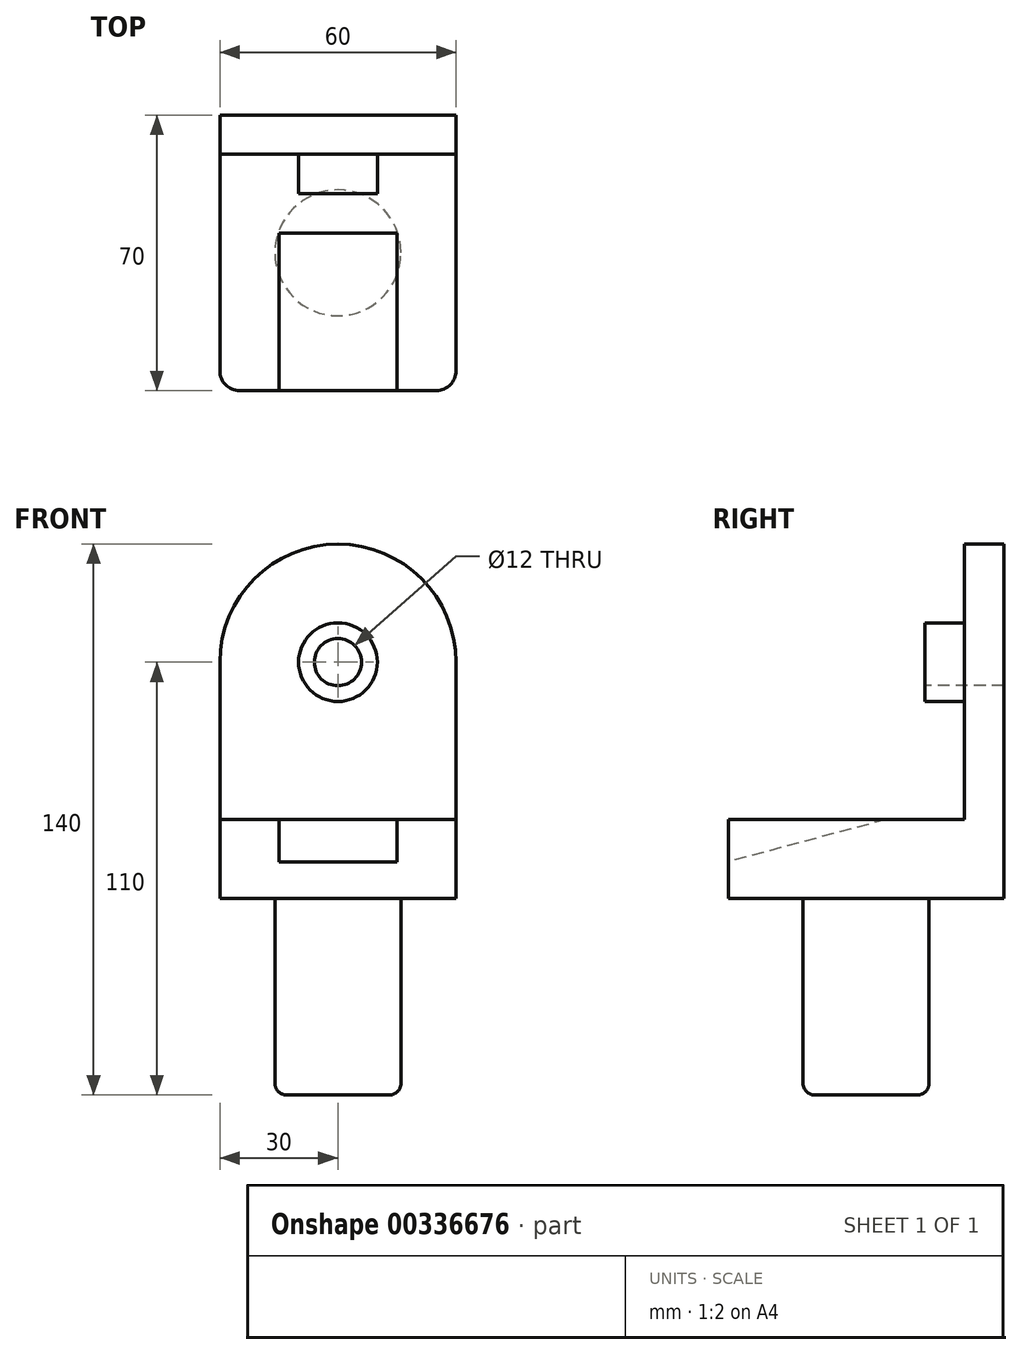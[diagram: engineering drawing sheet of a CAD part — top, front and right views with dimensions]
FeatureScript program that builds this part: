
annotation { "Feature Type Name" : "Feature", "Feature Type Description" : "" }
export const myFeature = defineFeature(function(context is Context, id is Id, definition is map)
    precondition{}
    {
        {
            var Q0;
            Q0=qCreatedBy(makeId("Top.planeOp"),FACE);
            var sketch = newSketch(context, id + "F0", { "sketchPlane" : qUnion([Q0])});
            skCircle(sketch, "E0", {"center": v(0, 0) * mm, "radius": 16 * mm});
            skSolve(sketch);
        }
        {
            var Q0;
            Q0 = qSketchRegion(id + "F0", true);
            extrude(context, id + "F1", {"entities" : qUnion([Q0]), "depth" : 50 * mm});
        }
        {
            var Q0;
            Q0=makeQuery(id+"F1.opExtrude","CAP_FACE",FACE,{"disambiguationData":[OSD([sQuery(id+"F0.wireOp",EDGE,"E0")])],"isStart":false});
            cPlane(context, id + "F2", {"entities" : qUnion([Q0]), "cplaneType" : CPlaneType.OFFSET, "offset" : 0 * mm, "width" : 150 * mm, "height" : 150 * mm});
        }
        {
            var Q0;
            Q0=qCreatedBy(id+"F2.planeOp",FACE);
            var sketch = newSketch(context, id + "F3", { "sketchPlane" : qUnion([Q0])});
            skLineSegment(sketch, "E1", {"start": v(-30, 35) * mm, "end": v(30, 35) * mm});
            skLineSegment(sketch, "E2", {"start": v(30, 35) * mm, "end": v(30, -35) * mm});
            skLineSegment(sketch, "E3", {"start": v(30, -35) * mm, "end": v(15, -35) * mm});
            skLineSegment(sketch, "E4", {"start": v(-30, -35) * mm, "end": v(-30, 35) * mm});
            skLineSegment(sketch, "E5.trimOffspring", {"start": v(-15, -35) * mm, "end": v(-30, -35) * mm});
            skLineSegment(sketch, "E6", {"start": v(-15, 5) * mm, "end": v(15, 5) * mm});
            skLineSegment(sketch, "E7", {"start": v(15, -35) * mm, "end": v(15, 5) * mm});
            skLineSegment(sketch, "E8", {"start": v(-15, -35) * mm, "end": v(-15, 5) * mm});
            skSolve(sketch);
        }
        {
            var Q0;
            Q0=makeQuery(id+"F1.opExtrude","CAP_EDGE",EDGE,{"disambiguationData":[OSD([sQuery(id+"F0.wireOp",EDGE,"E0")])],"isStart":true});
            fillet(context, id + "F4", {"entities" : qUnion([Q0]), "radius" : 3 * mm, "tangentPropagation" : true, "allowEdgeOverflow" : false});
        }
        {
            var Q0;
            Q0=qCreatedBy(id+"F2.planeOp",FACE);
            var sketch = newSketch(context, id + "F5", { "sketchPlane" : qUnion([Q0])});
            skLineSegment(sketch, "E9", {"start": v(15, 5) * mm, "end": v(15, -35) * mm});
            skLineSegment(sketch, "E10", {"start": v(15, -35) * mm, "end": v(-15, -35) * mm});
            skLineSegment(sketch, "E11", {"start": v(-15, -35) * mm, "end": v(-15, 5) * mm});
            skLineSegment(sketch, "E12", {"start": v(-15, 5) * mm, "end": v(15, 5) * mm});
            skSolve(sketch);
        }
        {
            var Q0;
            Q0 = qSketchRegion(id + "F5", true);
            extrude(context, id + "F6", {"entities" : qUnion([Q0]), "operationType" : NewBodyOperationType.ADD, "depth" : 20 * mm});
        }
        {
            var Q0;
            Q0=qCreatedBy(makeId("Right.planeOp"),FACE);
            var sketch = newSketch(context, id + "F7", { "sketchPlane" : qUnion([Q0])});
            skLineSegment(sketch, "E13", {"start": v(0, 70) * mm, "end": v(5, 70) * mm});
            skLineSegment(sketch, "E14", {"start": v(5, 70) * mm, "end": v(-35, 59.28) * mm});
            skLineSegment(sketch, "E15", {"start": v(5, 70) * mm, "end": v(-35, 70) * mm});
            skLineSegment(sketch, "E16", {"start": v(-35, 70) * mm, "end": v(-35, 59.28) * mm});
            skSolve(sketch);
        }
        {
            var Q0;
            Q0 = qSketchRegion(id + "F7", true);
            extrude(context, id + "F8", {"entities" : qUnion([Q0]), "operationType" : NewBodyOperationType.REMOVE, "endBound" : BoundingType.SYMMETRIC, "oppositeDirection" : true, "depth" : 30 * mm});
        }
        {
            var Q0;
            Q0=makeQuery(id+"F3.imprint","IMPRINT",FACE,{"disambiguationData":[TD([[makeQuery(id+"F3.imprint","IMPRINT",EDGE,{"derivedFrom":sQuery(id+"F3.wireOp",EDGE,"E1")}),-1.0]])]});
            extrude(context, id + "F9", {"entities" : qUnion([Q0]), "operationType" : NewBodyOperationType.ADD, "depth" : 20 * mm});
        }
        {
            var Q0;
            Q0=makeQuery(id+"F9.opExtrude","CAP_FACE",FACE,{"disambiguationData":[OSD([sQuery(id+"F3.wireOp",EDGE,"E1"),sQuery(id+"F3.wireOp",EDGE,"E2"),sQuery(id+"F3.wireOp",EDGE,"E3"),sQuery(id+"F3.wireOp",EDGE,"E4"),sQuery(id+"F3.wireOp",EDGE,"E5.trimOffspring"),sQuery(id+"F3.wireOp",EDGE,"E6"),sQuery(id+"F3.wireOp",EDGE,"E7"),sQuery(id+"F3.wireOp",EDGE,"E8")])],"isStart":false});
            cPlane(context, id + "F10", {"entities" : qUnion([Q0]), "cplaneType" : CPlaneType.OFFSET, "offset" : 0 * mm, "width" : 150 * mm, "height" : 150 * mm});
        }
        {
            var Q0;
            Q0=qCreatedBy(id+"F10.planeOp",FACE);
            var sketch = newSketch(context, id + "F11", { "sketchPlane" : qUnion([Q0])});
            skLineSegment(sketch, "E17", {"start": v(30, 35) * mm, "end": v(30, 25) * mm});
            skLineSegment(sketch, "E18", {"start": v(30, 25) * mm, "end": v(-30, 25) * mm});
            skLineSegment(sketch, "E19", {"start": v(-30, 25) * mm, "end": v(-30, 35) * mm});
            skLineSegment(sketch, "E20", {"start": v(-30, 35) * mm, "end": v(30, 35) * mm});
            skSolve(sketch);
        }
        {
            var Q0;
            Q0 = qSketchRegion(id + "F11", true);
            extrude(context, id + "F12", {"entities" : qUnion([Q0]), "operationType" : NewBodyOperationType.ADD, "depth" : 70 * mm});
        }
        {
            var Q0;
            Q0=makeQuery(id+"F12.opExtrude","CAP_EDGE",EDGE,{"disambiguationData":[OSD([sQuery(id+"F11.wireOp",EDGE,"E19")])],"isStart":false});
            var Q1;
            Q1=makeQuery(id+"F12.opExtrude","CAP_EDGE",EDGE,{"disambiguationData":[OSD([sQuery(id+"F11.wireOp",EDGE,"E17")])],"isStart":false});
            fillet(context, id + "F13", {"entities" : qUnion([Q0, Q1]), "radius" : 30 * mm, "tangentPropagation" : true, "allowEdgeOverflow" : false});
        }
        {
            var Q0;
            Q0=makeQuery(id+"F12.opExtrude","SWEPT_FACE",FACE,{"disambiguationData":[OSD([sQuery(id+"F11.wireOp",EDGE,"E18")])]});
            cPlane(context, id + "F14", {"entities" : qUnion([Q0]), "cplaneType" : CPlaneType.OFFSET, "offset" : 0 * mm, "width" : 150 * mm, "height" : 150 * mm});
        }
        {
            var Q0;
            Q0=qCreatedBy(id+"F14.planeOp",FACE);
            var sketch = newSketch(context, id + "F15", { "sketchPlane" : qUnion([Q0])});
            skLineSegment(sketch, "E21", {"start": v(0, 0) * mm, "end": v(0, 110) * mm});
            skCircle(sketch, "E22", {"center": v(0, 110) * mm, "radius": 10 * mm});
            skSolve(sketch);
        }
        {
            var Q0;
            Q0 = qSketchRegion(id + "F15", true);
            extrude(context, id + "F16", {"entities" : qUnion([Q0]), "operationType" : NewBodyOperationType.ADD, "depth" : 10 * mm});
        }
        {
            var Q0;
            Q0=makeQuery(id+"F16.opExtrude","CAP_FACE",FACE,{"disambiguationData":[OSD([sQuery(id+"F15.wireOp",EDGE,"E22")])],"isStart":false});
            cPlane(context, id + "F17", {"entities" : qUnion([Q0]), "cplaneType" : CPlaneType.OFFSET, "offset" : 0 * mm, "width" : 150 * mm, "height" : 150 * mm});
        }
        {
            var Q0;
            Q0=qCreatedBy(id+"F17.planeOp",FACE);
            var sketch = newSketch(context, id + "F18", { "sketchPlane" : qUnion([Q0])});
            skLineSegment(sketch, "E23", {"start": v(0, 0) * mm, "end": v(0, 110) * mm, "construction": true});
            skCircle(sketch, "E24", {"center": v(0, 110) * mm, "radius": 6 * mm});
            skSolve(sketch);
        }
        {
            var Q0;
            Q0 = qSketchRegion(id + "F18", true);
            extrude(context, id + "F19", {"entities" : qUnion([Q0]), "operationType" : NewBodyOperationType.REMOVE, "oppositeDirection" : true, "depth" : 50 * mm});
        }
        {
            var Q0;
            Q0=makeQuery(id+"F9.opExtrude","SWEPT_EDGE",EDGE,{"disambiguationData":[OSD([sQuery(id+"F3.wireOp",EDGE,"E4"),sQuery(id+"F3.wireOp",EDGE,"E5.trimOffspring")])]});
            var Q1;
            Q1=makeQuery(id+"F9.opExtrude","SWEPT_EDGE",EDGE,{"disambiguationData":[OSD([sQuery(id+"F3.wireOp",EDGE,"E2"),sQuery(id+"F3.wireOp",EDGE,"E3")])]});
            fillet(context, id + "F20", {"entities" : qUnion([Q0, Q1]), "radius" : 5 * mm, "tangentPropagation" : true, "allowEdgeOverflow" : false});
        }
    });
